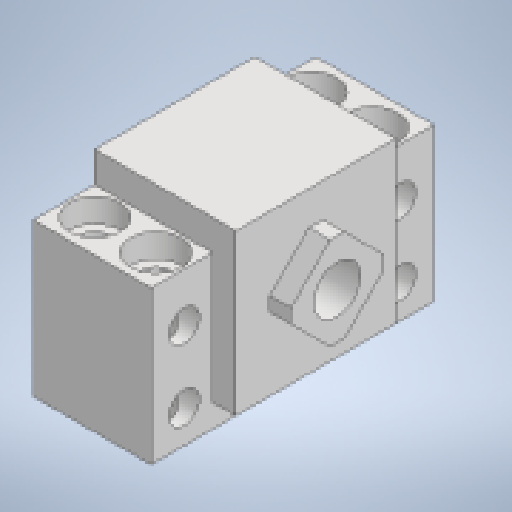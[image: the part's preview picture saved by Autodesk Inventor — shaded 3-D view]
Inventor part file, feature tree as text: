
AUTODESK INVENTOR PART (.ipt)
format: ipt  version: 2023 (Build 270158000, 158)  size: 251,904 bytes
history: native  units: mm
features: extrude x5, sketch x5, pattern_linear x1
ambient origin geometry x8: Origin, YZ Plane, XZ Plane, XY Plane, X Axis, Y Axis, Z Axis, Center Point
bodies: Solid1 (feature_tree)
feature tree (11):
  extrude  "Extrusion1"  Depth=6.6mm
  extrude  "Extrusion2"  Depth=46.0mm
  extrude  "Extrusion3"  Depth=32.5mm
  extrude  "Extrusion4"  Depth=39.0mm
  extrude  "Extrusion5"  Depth=10.0mm TaperAngle=0.0deg
  pattern_linear  "Rectangular Pattern1"  Spacing1=5.0mm  [1 undecoded]
  sketch  "Sketch1"  dims[d0=60.0mm d1=6.6mm]
  sketch  "Sketch2"  dims[d2=18.0mm d3=46.0mm]
  sketch  "Sketch3"  dims[d4=25.0mm d5=32.5mm]
  sketch  "Sketch4"  dims[d6=34.0mm d7=39.0mm]
  sketch  "Sketch5"  dims[d8=10.0mm d9=25.0mm d10=0.0mm d11=5.0mm d12=0.0mm d14=135.0deg d15=16.0mm d16=3.0mm d17=4.5mm d18=0.0mm d19=10.8mm d20=6.0mm d21=7.0mm d22=5.0mm d23=0.0mm d24=6.6mm d25=5.0mm d26=0.0mm d27=20.0mm d29=13.0mm d30=20.0mm d32=-46.0mm]
note: 1 required parameter value undecoded (feature->parameter linkage not recoverable at this tier; creation-order binding heuristic only, values carry confidence <= 0.55)
